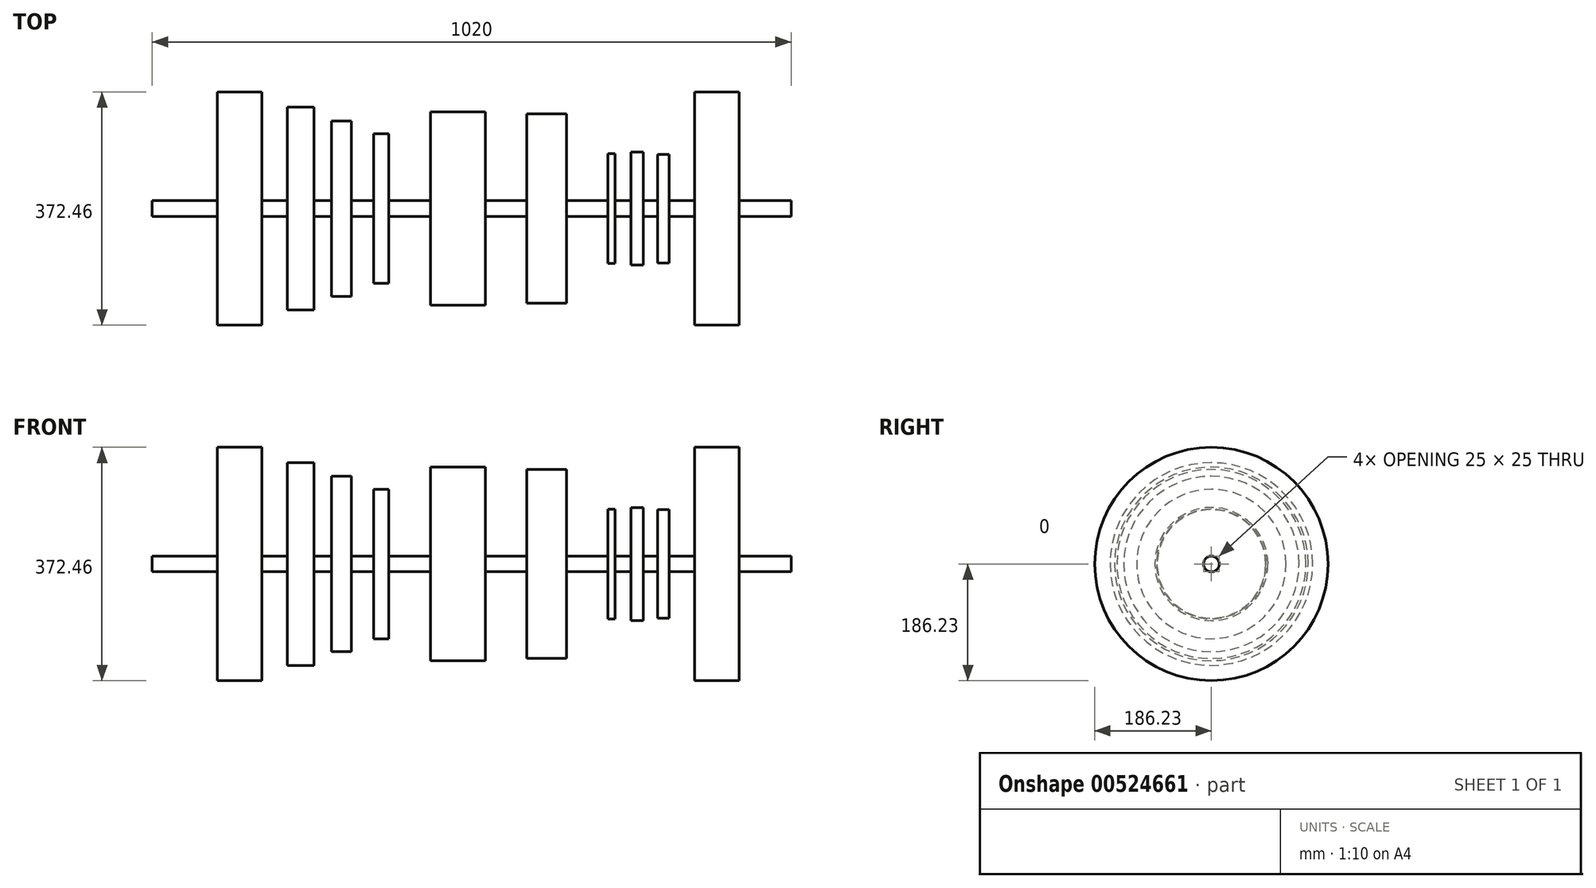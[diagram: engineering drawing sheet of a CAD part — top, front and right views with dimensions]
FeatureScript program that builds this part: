
annotation { "Feature Type Name" : "Feature", "Feature Type Description" : "" }
export const myFeature = defineFeature(function(context is Context, id is Id, definition is map)
    precondition{}
    {
        {
            var Q0;
            Q0=qCreatedBy(makeId("Right.planeOp"),FACE);
            var sketch = newSketch(context, id + "F0", { "sketchPlane" : qUnion([Q0])});
            skCircle(sketch, "E0", {"center": v(0, 0) * mm, "radius": 12.5 * mm});
            skSolve(sketch);
        }
        {
            var Q0;
            Q0=makeQuery(id+"F0.imprint","IMPRINT",FACE,{"disambiguationData":[TD([[makeQuery(id+"F0.imprint","IMPRINT",EDGE,{"derivedFrom":sQuery(id+"F0.wireOp",EDGE,"E0")}),1.0]])]});
            extrude(context, id + "F1", {"entities" : qUnion([Q0]), "depth" : 1020 * mm, "offsetDistance" : 25 * mm, "symmetric" : true});
        }
        {
            var Q0;
            Q0=qCreatedBy(makeId("Top.planeOp"),FACE);
            var sketch = newSketch(context, id + "F2", { "sketchPlane" : qUnion([Q0])});
            skLineSegment(sketch, "E1", {"start": v(427.32, 0) * mm, "end": v(427.32, 186.23) * mm});
            skLineSegment(sketch, "E2", {"start": v(427.32, 186.23) * mm, "end": v(355.8, 186.23) * mm});
            skLineSegment(sketch, "E3", {"start": v(355.8, 186.23) * mm, "end": v(355.8, 0) * mm});
            skLineSegment(sketch, "E4", {"start": v(355.8, 0) * mm, "end": v(315.07, 0) * mm});
            skLineSegment(sketch, "E5", {"start": v(315.07, 0) * mm, "end": v(315.07, 86.65) * mm});
            skLineSegment(sketch, "E6", {"start": v(315.07, 86.65) * mm, "end": v(296.97, 86.65) * mm});
            skLineSegment(sketch, "E7", {"start": v(296.97, 86.65) * mm, "end": v(296.97, 0) * mm});
            skLineSegment(sketch, "E8", {"start": v(296.97, 0) * mm, "end": v(274.34, 0) * mm});
            skLineSegment(sketch, "E9", {"start": v(274.34, 0) * mm, "end": v(274.34, 90.27) * mm});
            skLineSegment(sketch, "E10", {"start": v(274.34, 90.27) * mm, "end": v(254.42, 90.27) * mm});
            skLineSegment(sketch, "E11", {"start": v(254.42, 90.27) * mm, "end": v(254.42, 0) * mm});
            skLineSegment(sketch, "E12", {"start": v(254.42, 0) * mm, "end": v(229.08, 0) * mm});
            skLineSegment(sketch, "E13", {"start": v(229.08, 0) * mm, "end": v(229.08, 87.56) * mm});
            skLineSegment(sketch, "E14", {"start": v(229.08, 87.56) * mm, "end": v(217.3, 87.56) * mm});
            skLineSegment(sketch, "E15", {"start": v(217.3, 87.56) * mm, "end": v(217.3, 0) * mm});
            skLineSegment(sketch, "E16", {"start": v(217.3, 0) * mm, "end": v(151.23, 0) * mm});
            skLineSegment(sketch, "E17", {"start": v(151.23, 0) * mm, "end": v(151.23, 150.92) * mm});
            skLineSegment(sketch, "E18", {"start": v(151.23, 150.92) * mm, "end": v(87.86, 150.92) * mm});
            skLineSegment(sketch, "E19", {"start": v(87.86, 150.92) * mm, "end": v(87.86, 0) * mm});
            skLineSegment(sketch, "E20", {"start": v(87.86, 0) * mm, "end": v(21.78, 0) * mm});
            skLineSegment(sketch, "E21", {"start": v(21.78, 0) * mm, "end": v(21.78, 154.55) * mm});
            skLineSegment(sketch, "E22", {"start": v(21.78, 154.55) * mm, "end": v(-66.02, 154.55) * mm});
            skLineSegment(sketch, "E23", {"start": v(-66.02, 154.55) * mm, "end": v(-66.02, 0) * mm});
            skLineSegment(sketch, "E24", {"start": v(-66.02, 0) * mm, "end": v(-132.1, 0) * mm});
            skLineSegment(sketch, "E25", {"start": v(-132.1, 0) * mm, "end": v(-132.1, 119.24) * mm});
            skLineSegment(sketch, "E26", {"start": v(-132.1, 119.24) * mm, "end": v(-156.55, 119.24) * mm});
            skLineSegment(sketch, "E27", {"start": v(-156.55, 119.24) * mm, "end": v(-156.55, 0) * mm});
            skLineSegment(sketch, "E28", {"start": v(-156.55, 0) * mm, "end": v(-191.85, 0) * mm});
            skLineSegment(sketch, "E29", {"start": v(-191.85, 0) * mm, "end": v(-191.85, 140.06) * mm});
            skLineSegment(sketch, "E30", {"start": v(-191.85, 140.06) * mm, "end": v(-223.53, 140.06) * mm});
            skLineSegment(sketch, "E31", {"start": v(-223.53, 140.06) * mm, "end": v(-223.53, 0) * mm});
            skLineSegment(sketch, "E32", {"start": v(-223.53, 0) * mm, "end": v(-251.6, 0) * mm});
            skLineSegment(sketch, "E33", {"start": v(-251.6, 0) * mm, "end": v(-251.6, 161.79) * mm});
            skLineSegment(sketch, "E34", {"start": v(-251.6, 161.79) * mm, "end": v(-294.14, 161.79) * mm});
            skLineSegment(sketch, "E35", {"start": v(-294.14, 161.79) * mm, "end": v(-294.14, 0) * mm});
            skLineSegment(sketch, "E36", {"start": v(-294.14, 0) * mm, "end": v(-334.87, 0) * mm});
            skLineSegment(sketch, "E37", {"start": v(-334.87, 0) * mm, "end": v(-334.87, 186.23) * mm});
            skLineSegment(sketch, "E38", {"start": v(-334.87, 186.23) * mm, "end": v(-406.39, 186.23) * mm});
            skLineSegment(sketch, "E39", {"start": v(-406.39, 186.23) * mm, "end": v(-406.39, 0) * mm});
            skLineSegment(sketch, "E40", {"start": v(-406.39, 0) * mm, "end": v(427.32, 0) * mm});
            skSolve(sketch);
        }
        {
            var Q0;
            Q0 = qSketchRegion(id + "F2", true);
            var Q1;
            Q1=sQuery(id+"F2.wireOp",EDGE,"E40");
            revolve(context, id + "F3", {"operationType" : NewBodyOperationType.ADD, "entities" : qUnion([Q0]), "axis" : qUnion([Q1]), "revolveType" : RevolveType.FULL});
        }
    });
